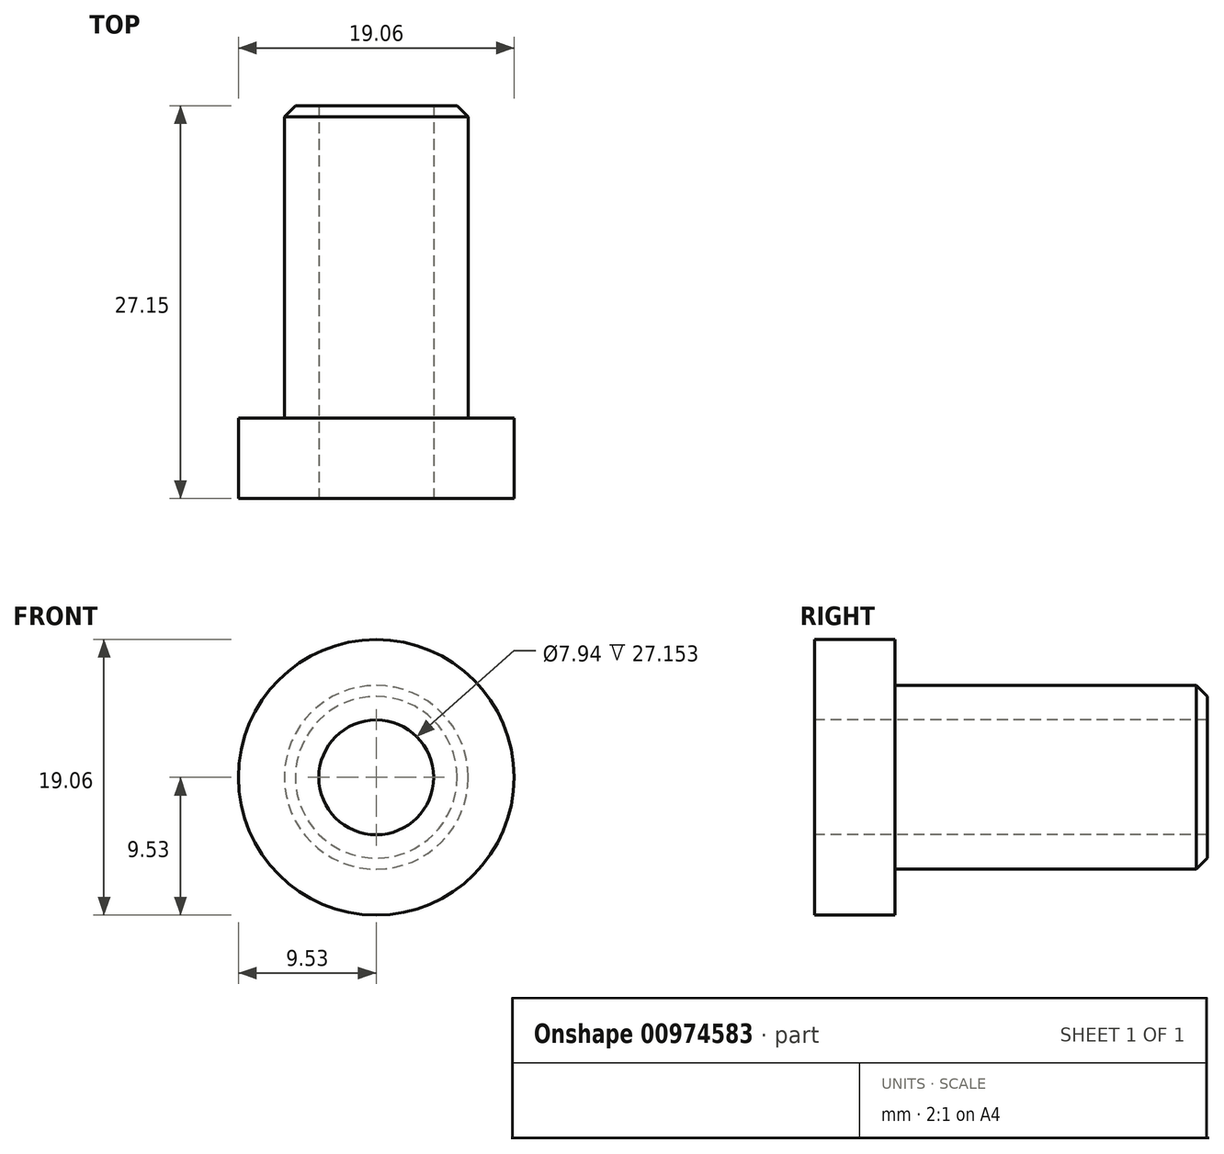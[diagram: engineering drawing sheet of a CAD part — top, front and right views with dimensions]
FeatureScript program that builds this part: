
annotation { "Feature Type Name" : "Feature", "Feature Type Description" : "" }
export const myFeature = defineFeature(function(context is Context, id is Id, definition is map)
    precondition{}
    {
        {
            var Q0;
            Q0=qCreatedBy(makeId("Front.planeOp"),FACE);
            var sketch = newSketch(context, id + "F0", { "sketchPlane" : qUnion([Q0])});
            skCircle(sketch, "E0", {"center": v(0, 0) * mm, "radius": 9.52 * mm});
            skSolve(sketch);
        }
        {
            var Q0;
            Q0=makeQuery(id+"F0.imprint","IMPRINT",FACE,{"disambiguationData":[TD([[makeQuery(id+"F0.imprint","IMPRINT",EDGE,{"derivedFrom":sQuery(id+"F0.wireOp",EDGE,"E0")}),1.0]])]});
            extrude(context, id + "F1", {"entities" : qUnion([Q0]), "endBound" : BoundingType.SYMMETRIC, "depth" : (5 + (9 / 16)) * mm, "offsetDistance" : 25.4 * mm});
        }
        {
            var Q0;
            Q0=makeQuery(id+"F1.opExtrude","CAP_FACE",FACE,{"disambiguationData":[OSD([sQuery(id+"F0.wireOp",EDGE,"E0")])],"isStart":false});
            var sketch = newSketch(context, id + "F2", { "sketchPlane" : qUnion([Q0])});
            skPoint(sketch, "E1", {"position": v(0, 0) * mm});
            skSolve(sketch);
        }
        {
            var Q0;
            Q0=sQuery(id+"F2.wireOp",VERTEX,"E1");
            var Q1;
            Q1=makeQuery(id+"F1.opExtrude","SWEPT_BODY",BODY,{"disambiguationData":[OSD([sQuery(id+"F0.wireOp",EDGE,"E0")])]});
            hole(context, id + "F3", {"style" : HoleStyle.SIMPLE, "endStyle" : HoleEndStyle.BLIND, "standardTappedOrClearance" : lookupTablePath({ "standard" : "ANSI", "engagement" : "75%", "pitch" : "16 tpi", "size" : "3/8", "type" : "Tapped" }), "standardBlindInLast" : lookupTablePath({ "standard" : "ANSI", "fit" : "Free", "engagement" : "75%", "pitch" : "16 tpi", "size" : "3/8", "type" : "Clearance & tapped" }), "holeDiameter" : 7.94 * mm, "majorDiameter" : 9.52 * mm, "showTappedDepth" : true, "holeDepth" : 31.75 * mm, "isTappedThrough" : true, "tappedDepth" : 26.99 * mm, "tapClearance" : 3, "startFromSketch" : true, "locations" : qUnion([Q0]), "scope" : qUnion([Q1])});
        }
        {
            var Q0;
            Q0=makeQuery(id+"F1.opExtrude","CAP_FACE",FACE,{"disambiguationData":[OSD([sQuery(id+"F0.wireOp",EDGE,"E0")])],"isStart":true});
            var sketch = newSketch(context, id + "F4", { "sketchPlane" : qUnion([Q0])});
            skCircle(sketch, "E2", {"center": v(0, 0) * mm, "radius": 6.35 * mm});
            skSolve(sketch);
        }
        {
            var Q0;
            Q0=makeQuery(id+"F4.imprint","IMPRINT",FACE,{"disambiguationData":[TD([[makeQuery(id+"F4.imprint","IMPRINT",EDGE,{"derivedFrom":sQuery(id+"F4.wireOp",EDGE,"E2")}),1.0]])]});
            extrude(context, id + "F5", {"entities" : qUnion([Q0]), "operationType" : NewBodyOperationType.ADD, "depth" : 21.59 * mm, "offsetDistance" : 25.4 * mm});
        }
        {
            var Q0;
            Q0=makeQuery(id+"F5.opExtrude","CAP_EDGE",EDGE,{"disambiguationData":[OSD([sQuery(id+"F4.wireOp",EDGE,"E2")])],"isStart":false});
            chamfer(context, id + "F6", {"entities" : qUnion([Q0]), "width" : 0.76 * mm, "tangentPropagation" : true});
        }
    });
